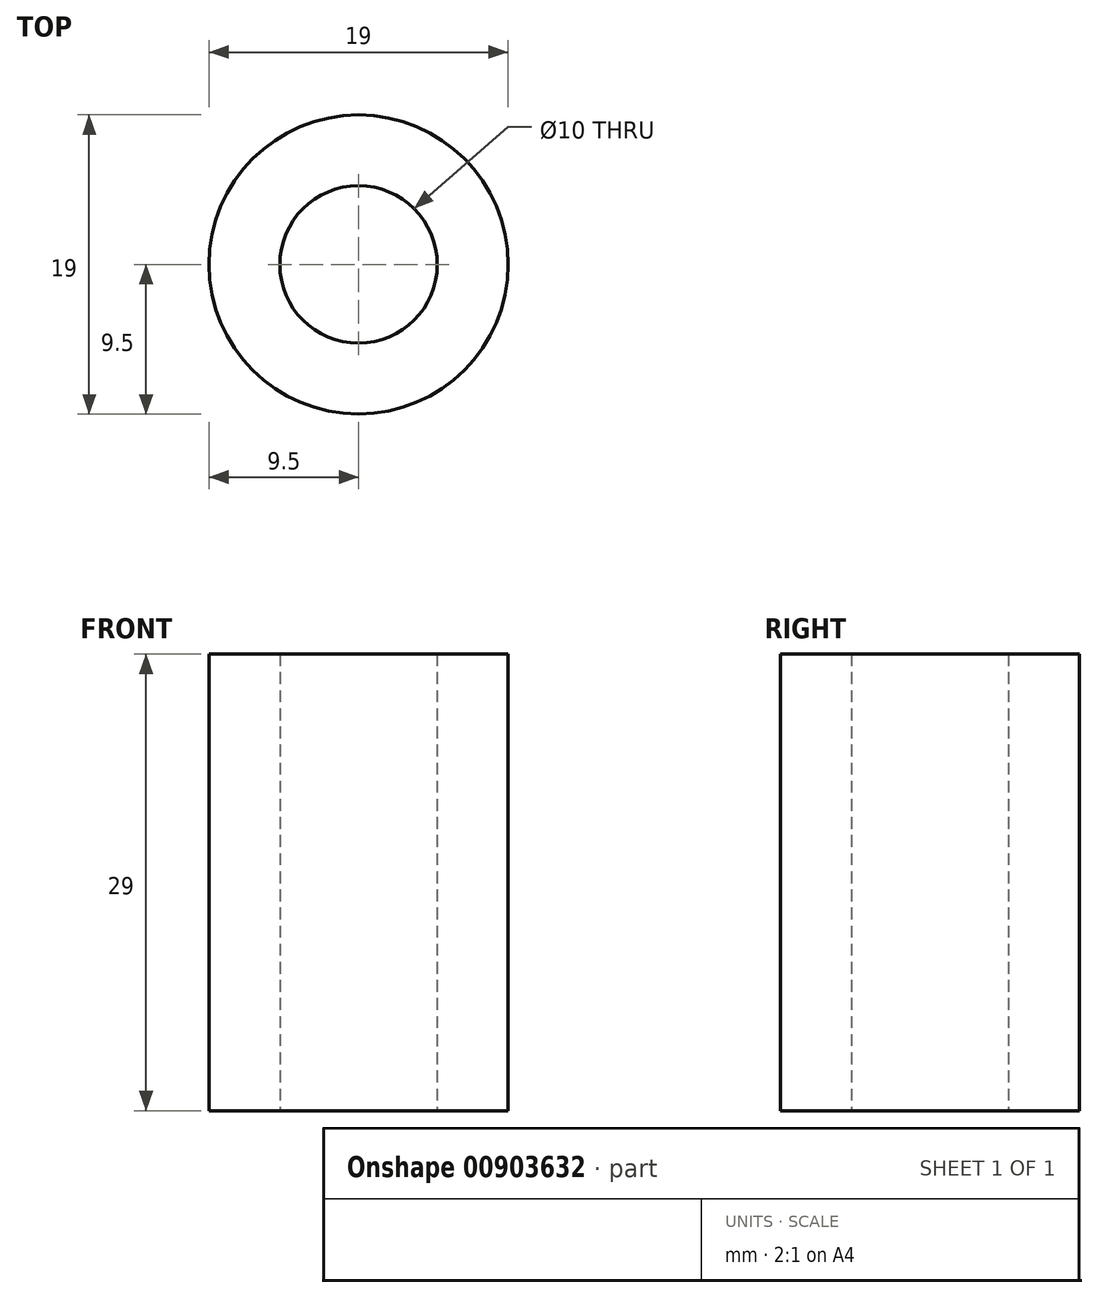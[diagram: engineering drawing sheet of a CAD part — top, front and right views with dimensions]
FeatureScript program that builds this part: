
annotation { "Feature Type Name" : "Feature", "Feature Type Description" : "" }
export const myFeature = defineFeature(function(context is Context, id is Id, definition is map)
    precondition{}
    {
        {
            var Q0;
            Q0=qCreatedBy(makeId("Top.planeOp"),FACE);
            var sketch = newSketch(context, id + "F0", { "sketchPlane" : qUnion([Q0])});
            skCircle(sketch, "E0", {"center": v(0, 0) * mm, "radius": 9.5 * mm});
            skCircle(sketch, "E1", {"center": v(0, 0) * mm, "radius": 5 * mm});
            skSolve(sketch);
        }
        {
            var Q0;
            Q0=qSketchRegion(id+"F0",true);
            extrude(context, id + "F1", {"entities" : qUnion([Q0]), "depth" : 29 * mm});
        }
    });
